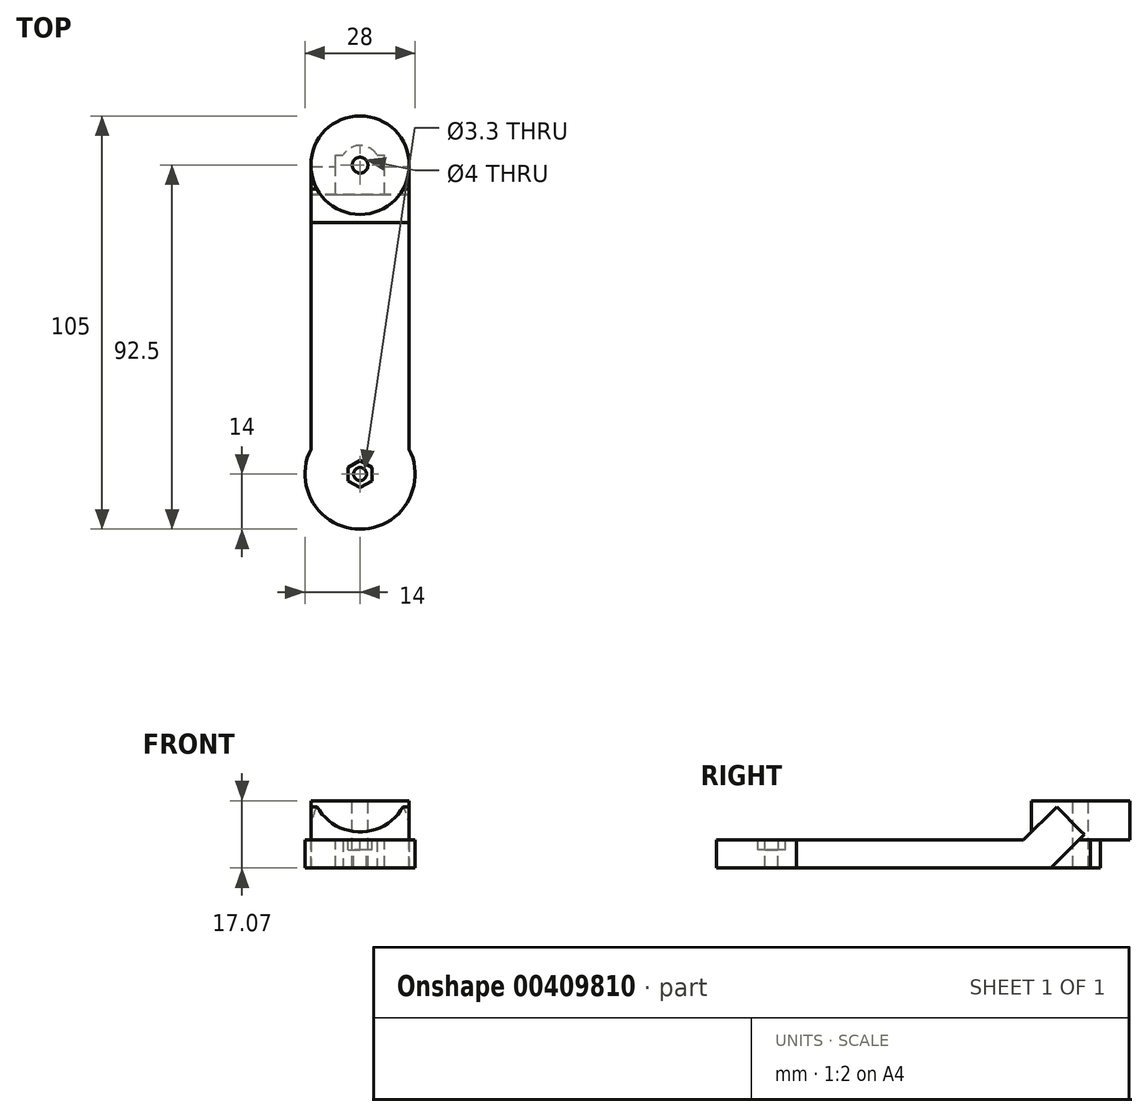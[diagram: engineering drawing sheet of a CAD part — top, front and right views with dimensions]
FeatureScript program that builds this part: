
annotation { "Feature Type Name" : "Feature", "Feature Type Description" : "" }
export const myFeature = defineFeature(function(context is Context, id is Id, definition is map)
    precondition{}
    {
        {
            var Q0;
            Q0=qCreatedBy(makeId("Top.planeOp"),FACE);
            var sketch = newSketch(context, id + "F0", { "sketchPlane" : qUnion([Q0])});
            skLineSegment(sketch, "E0.bottom", {"start": v(12.5, -37.5) * mm, "end": v(-12.5, -37.5) * mm});
            skLineSegment(sketch, "E0.top", {"start": v(12.5, 37.5) * mm, "end": v(-12.5, 37.5) * mm});
            skLineSegment(sketch, "E0.left", {"start": v(12.5, -37.5) * mm, "end": v(12.5, 37.5) * mm});
            skLineSegment(sketch, "E0.right", {"start": v(-12.5, -37.5) * mm, "end": v(-12.5, 37.5) * mm});
            skPoint(sketch, "E0.middle", {"position": v(0, 0) * mm});
            skLineSegment(sketch, "E1", {"start": v(-12.5, 37.5) * mm, "end": v(0, 37.5) * mm, "construction": true});
            skLineSegment(sketch, "E2", {"start": v(12.5, 37.5) * mm, "end": v(0, 37.5) * mm, "construction": true});
            skPoint(sketch, "E3.oppositeSnap0", {"position": v(6.25, 37.5) * mm});
            skLineSegment(sketch, "E3.bottom", {"start": v(-6.25, 37.5) * mm, "end": v(6.25, 37.5) * mm});
            skLineSegment(sketch, "E3.top", {"start": v(-6.25, 47.5) * mm, "end": v(6.25, 47.5) * mm});
            skLineSegment(sketch, "E3.left", {"start": v(-6.25, 37.5) * mm, "end": v(-6.25, 47.5) * mm});
            skLineSegment(sketch, "E3.right", {"start": v(6.25, 37.5) * mm, "end": v(6.25, 47.5) * mm});
            skLineSegment(sketch, "E4", {"start": v(6.25, 47.5) * mm, "end": v(6.25, 45) * mm, "construction": true});
            skLineSegment(sketch, "E5", {"start": v(6.25, 45) * mm, "end": v(0, 45) * mm, "construction": true});
            skCircle(sketch, "E6", {"center": v(0, 45) * mm, "radius": 2.5 * mm, "construction": true});
            skCircle(sketch, "E7", {"center": v(0, 45) * mm, "radius": 5 * mm});
            skSolve(sketch);
        }
        {
            var Q0;
            Q0=qSketchRegion(id+"F0",true);
            extrude(context, id + "F1", {"entities" : qUnion([Q0]), "depth" : 7 * mm});
        }
        {
            var Q0;
            Q0=makeQuery(id+"F1.opExtrude","CAP_FACE",FACE,{"disambiguationData":[OSD([sQuery(id+"F0.wireOp",EDGE,"E0.bottom"),sQuery(id+"F0.wireOp",EDGE,"E0.top"),sQuery(id+"F0.wireOp",EDGE,"E0.left"),sQuery(id+"F0.wireOp",EDGE,"E0.right"),sQuery(id+"F0.wireOp",EDGE,"E3.left"),sQuery(id+"F0.wireOp",EDGE,"E3.right"),sQuery(id+"F0.wireOp",EDGE,"E7")])],"isStart":false});
            var sketch = newSketch(context, id + "F2", { "sketchPlane" : qUnion([Q0])});
            skCircle(sketch, "E8", {"center": v(0, 45) * mm, "radius": 12.5 * mm});
            skSolve(sketch);
        }
        {
            var Q0;
            Q0=qSketchRegion(id+"F2",true);
            extrude(context, id + "F3", {"entities" : qUnion([Q0]), "operationType" : NewBodyOperationType.ADD, "depth" : 10 * mm});
        }
        {
            var Q0;
            Q0=makeQuery(id+"F1.opExtrude","CAP_FACE",FACE,{"disambiguationData":[OSD([sQuery(id+"F0.wireOp",EDGE,"E0.bottom"),sQuery(id+"F0.wireOp",EDGE,"E0.top"),sQuery(id+"F0.wireOp",EDGE,"E0.left"),sQuery(id+"F0.wireOp",EDGE,"E0.right"),sQuery(id+"F0.wireOp",EDGE,"E3.left"),sQuery(id+"F0.wireOp",EDGE,"E3.right"),sQuery(id+"F0.wireOp",EDGE,"E7")])],"isStart":false});
            var sketch = newSketch(context, id + "F4", { "sketchPlane" : qUnion([Q0])});
            skLineSegment(sketch, "E9", {"start": v(12.5, -37.5) * mm, "end": v(12.5, -29.5) * mm, "construction": true});
            skLineSegment(sketch, "E10", {"start": v(12.5, -29.5) * mm, "end": v(-12.5, -29.5) * mm, "construction": true});
            skLineSegment(sketch, "E11", {"start": v(12.5, -37.5) * mm, "end": v(-12.5, -29.5) * mm, "construction": true});
            skCircle(sketch, "E12", {"center": v(0, -33.5) * mm, "radius": 2 * mm});
            skSolve(sketch);
        }
        {
            var Q0;
            Q0=qSketchRegion(id+"F4",true);
            extrude(context, id + "F5", {"entities" : qUnion([Q0]), "operationType" : NewBodyOperationType.REMOVE, "endBound" : BoundingType.UP_TO_NEXT, "oppositeDirection" : true, "depth" : 25 * mm});
        }
        {
            var Q0;
            Q0=makeQuery(id+"F1.opExtrude","CAP_FACE",FACE,{"disambiguationData":[OSD([sQuery(id+"F0.wireOp",EDGE,"E0.bottom"),sQuery(id+"F0.wireOp",EDGE,"E0.top"),sQuery(id+"F0.wireOp",EDGE,"E0.left"),sQuery(id+"F0.wireOp",EDGE,"E0.right"),sQuery(id+"F0.wireOp",EDGE,"E3.left"),sQuery(id+"F0.wireOp",EDGE,"E3.right"),sQuery(id+"F0.wireOp",EDGE,"E7")])],"isStart":false});
            var sketch = newSketch(context, id + "F6", { "sketchPlane" : qUnion([Q0])});
            skLineSegment(sketch, "E13", {"start": v(12.5, 37.5) * mm, "end": v(-12.5, 37.5) * mm, "construction": true});
            skSolve(sketch);
        }
        {
            var Q0;
            Q0=sQuery(id+"F6.wireOp",EDGE,"E13");
            cPlane(context, id + "F7", {"entities" : qUnion([Q0]), "cplaneType" : CPlaneType.LINE_ANGLE, "offset" : 25 * mm, "angle" : 45 * degree, "width" : 150 * mm, "height" : 150 * mm});
        }
        {
            var Q0;
            Q0=qCreatedBy(id+"F7.planeOp",FACE);
            cPlane(context, id + "F8", {"entities" : qUnion([Q0]), "cplaneType" : CPlaneType.OFFSET, "offset" : 5 * mm, "width" : 150 * mm, "height" : 150 * mm});
        }
        {
            var Q0;
            Q0=qCreatedBy(id+"F8.planeOp",FACE);
            var sketch = newSketch(context, id + "F9", { "sketchPlane" : qUnion([Q0])});
            skLineSegment(sketch, "E14", {"start": v(12.5, 26.47) * mm, "end": v(-12.5, 26.47) * mm});
            skLineSegment(sketch, "E15.bottom", {"start": v(-12.5, 26.47) * mm, "end": v(12.5, 26.47) * mm});
            skLineSegment(sketch, "E15.top", {"start": v(-12.5, 38.47) * mm, "end": v(12.5, 38.47) * mm});
            skLineSegment(sketch, "E15.left", {"start": v(-12.5, 26.47) * mm, "end": v(-12.5, 38.47) * mm});
            skLineSegment(sketch, "E15.right", {"start": v(12.5, 26.47) * mm, "end": v(12.5, 38.47) * mm});
            skSolve(sketch);
        }
        {
            var Q0;
            Q0=qSketchRegion(id+"F9",true);
            var Q1;
            Q1=makeQuery(id+"F1.opExtrude","SWEPT_BODY",BODY,{"disambiguationData":[OSD([sQuery(id+"F0.wireOp",EDGE,"E0.bottom"),sQuery(id+"F0.wireOp",EDGE,"E0.top"),sQuery(id+"F0.wireOp",EDGE,"E0.left"),sQuery(id+"F0.wireOp",EDGE,"E0.right"),sQuery(id+"F0.wireOp",EDGE,"E3.left"),sQuery(id+"F0.wireOp",EDGE,"E3.right"),sQuery(id+"F0.wireOp",EDGE,"E7")])]});
            extrude(context, id + "F10", {"entities" : qUnion([Q0]), "operationType" : NewBodyOperationType.ADD, "oppositeDirection" : true, "endBoundEntityBody" : qUnion([Q1]), "depth" : 10 * mm});
        }
        {
            var Q0;
            Q0=makeQuery(id+"F3.opExtrude","CAP_FACE",FACE,{"disambiguationData":[OSD([sQuery(id+"F2.wireOp",EDGE,"E8")])],"isStart":false});
            var sketch = newSketch(context, id + "F11", { "sketchPlane" : qUnion([Q0])});
            skCircle(sketch, "E16", {"center": v(0, 45) * mm, "radius": 2 * mm});
            skSolve(sketch);
        }
        {
            var Q0;
            Q0=qSketchRegion(id+"F11",true);
            extrude(context, id + "F12", {"entities" : qUnion([Q0]), "operationType" : NewBodyOperationType.REMOVE, "endBound" : BoundingType.UP_TO_NEXT, "oppositeDirection" : true, "depth" : 25 * mm});
        }
        {
            var Q0;
            {var subQ0=sQuery(id+"F0.wireOp",EDGE,"E0.right");var subQ1=sQuery(id+"F0.wireOp",EDGE,"E0.left");var subQ2=sQuery(id+"F0.wireOp",EDGE,"E0.bottom");Q0=makeQuery(id+"F10.boolean.opBoolean","SPLIT",FACE,{"disambiguationData":[TD([makeQuery(id+"F1.opExtrude","SWEPT_FACE",FACE,{"disambiguationData":[OSD([subQ2])]})])],"derivedFrom":makeQuery(id+"F1.opExtrude","CAP_FACE",FACE,{"disambiguationData":[OSD([subQ2,sQuery(id+"F0.wireOp",EDGE,"E0.top"),subQ1,subQ0,sQuery(id+"F0.wireOp",EDGE,"E3.top"),sQuery(id+"F0.wireOp",EDGE,"E3.left"),sQuery(id+"F0.wireOp",EDGE,"E3.right"),sQuery(id+"F0.wireOp",EDGE,"E7")])],"isStart":true})});}
            var sketch = newSketch(context, id + "F13", { "sketchPlane" : qUnion([Q0])});
            skCircle(sketch, "E17", {"center": v(0, 33.5) * mm, "radius": 14 * mm});
            skSolve(sketch);
        }
        {
            var Q0;
            Q0=qSketchRegion(id+"F13",true);
            var Q1;
            Q1=makeQuery(id+"F1.opExtrude","CAP_FACE",FACE,{"disambiguationData":[OSD([sQuery(id+"F0.wireOp",EDGE,"E0.bottom"),sQuery(id+"F0.wireOp",EDGE,"E0.top"),sQuery(id+"F0.wireOp",EDGE,"E0.left"),sQuery(id+"F0.wireOp",EDGE,"E0.right"),sQuery(id+"F0.wireOp",EDGE,"E3.top"),sQuery(id+"F0.wireOp",EDGE,"E3.left"),sQuery(id+"F0.wireOp",EDGE,"E3.right"),sQuery(id+"F0.wireOp",EDGE,"E7")])],"isStart":false});
            extrude(context, id + "F14", {"entities" : qUnion([Q0]), "operationType" : NewBodyOperationType.ADD, "endBound" : BoundingType.UP_TO_SURFACE, "oppositeDirection" : true, "endBoundEntityFace" : qUnion([Q1]), "depth" : 25 * mm});
        }
        {
            var Q0;
            {var subQ0=sQuery(id+"F0.wireOp",EDGE,"E7");var subQ1=sQuery(id+"F0.wireOp",EDGE,"E3.right");var subQ2=sQuery(id+"F0.wireOp",EDGE,"E3.left");var subQ3=sQuery(id+"F0.wireOp",EDGE,"E3.top");var subQ4=sQuery(id+"F0.wireOp",EDGE,"E0.right");var subQ5=sQuery(id+"F0.wireOp",EDGE,"E0.left");var subQ6=sQuery(id+"F0.wireOp",EDGE,"E0.top");var subQ7=sQuery(id+"F0.wireOp",EDGE,"E0.bottom");Q0=makeQuery(id+"F14.boolean.opBoolean","MERGE",FACE,{"derivedFrom":[makeQuery(id+"F1.opExtrude","CAP_FACE",FACE,{"disambiguationData":[OSD([subQ7,subQ6,subQ5,subQ4,subQ3,subQ2,subQ1,subQ0])],"isStart":false}),makeQuery(id+"F14.opExtrude","CAP_FACE",FACE,{"disambiguationData":[OSD([subQ7,subQ6,subQ5,subQ4,subQ3,subQ2,subQ1,subQ0])],"isStart":false})]});}
            var sketch = newSketch(context, id + "F15", { "sketchPlane" : qUnion([Q0])});
            skCircle(sketch, "E18", {"center": v(0, -33.5) * mm, "radius": 1.65 * mm});
            skSolve(sketch);
        }
        {
            var Q0;
            Q0=qSketchRegion(id+"F15",true);
            extrude(context, id + "F16", {"entities" : qUnion([Q0]), "operationType" : NewBodyOperationType.REMOVE, "endBound" : BoundingType.UP_TO_NEXT, "oppositeDirection" : true, "depth" : 25 * mm});
        }
        {
            var Q0;
            {var subQ0=sQuery(id+"F0.wireOp",EDGE,"E7");var subQ1=sQuery(id+"F0.wireOp",EDGE,"E3.right");var subQ2=sQuery(id+"F0.wireOp",EDGE,"E3.left");var subQ3=sQuery(id+"F0.wireOp",EDGE,"E3.top");var subQ4=sQuery(id+"F0.wireOp",EDGE,"E0.right");var subQ5=sQuery(id+"F0.wireOp",EDGE,"E0.left");var subQ6=sQuery(id+"F0.wireOp",EDGE,"E0.top");var subQ7=sQuery(id+"F0.wireOp",EDGE,"E0.bottom");Q0=makeQuery(id+"F14.boolean.opBoolean","MERGE",FACE,{"derivedFrom":[makeQuery(id+"F1.opExtrude","CAP_FACE",FACE,{"disambiguationData":[OSD([subQ7,subQ6,subQ5,subQ4,subQ3,subQ2,subQ1,subQ0])],"isStart":false}),makeQuery(id+"F14.opExtrude","CAP_FACE",FACE,{"disambiguationData":[OSD([subQ7,subQ6,subQ5,subQ4,subQ3,subQ2,subQ1,subQ0])],"isStart":false})]});}
            var sketch = newSketch(context, id + "F17", { "sketchPlane" : qUnion([Q0])});
            skCircle(sketch, "E19.cCircle", {"center": v(0, -33.5) * mm, "radius": 3 * mm, "construction": true});
            skLineSegment(sketch, "E19.0", {"start": v(3, -35.23) * mm, "end": v(0, -36.96) * mm});
            skLineSegment(sketch, "E19.1", {"start": v(0, -36.96) * mm, "end": v(-3, -35.23) * mm});
            skLineSegment(sketch, "E19.2", {"start": v(-3, -35.23) * mm, "end": v(-3, -31.77) * mm});
            skLineSegment(sketch, "E19.3", {"start": v(-3, -31.77) * mm, "end": v(0, -30.04) * mm});
            skLineSegment(sketch, "E19.4", {"start": v(0, -30.04) * mm, "end": v(3, -31.77) * mm});
            skLineSegment(sketch, "E19.5", {"start": v(3, -31.77) * mm, "end": v(3, -35.23) * mm});
            skPoint(sketch, "E19.0.midPoint", {"position": v(1.5, -36.1) * mm});
            skSolve(sketch);
        }
        {
            var Q0;
            Q0=qSketchRegion(id+"F17",true);
            extrude(context, id + "F18", {"entities" : qUnion([Q0]), "operationType" : NewBodyOperationType.REMOVE, "oppositeDirection" : true, "depth" : 2.5 * mm});
        }
    });
